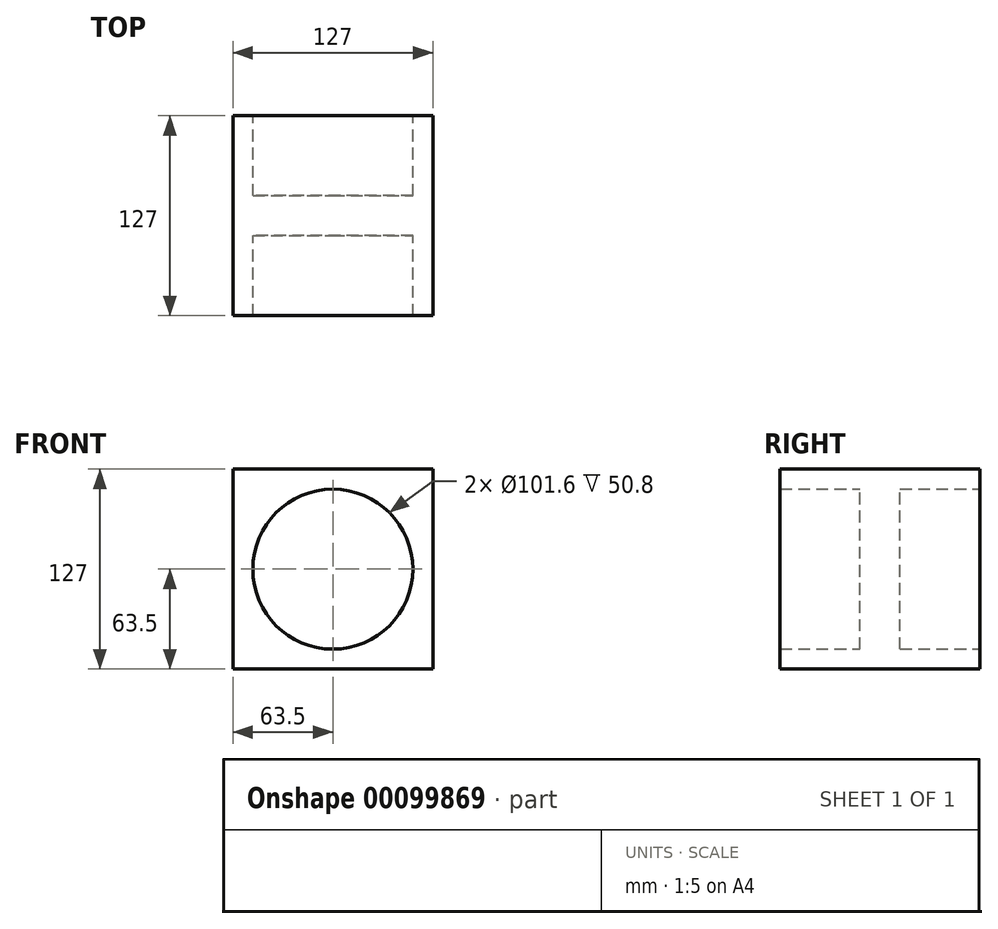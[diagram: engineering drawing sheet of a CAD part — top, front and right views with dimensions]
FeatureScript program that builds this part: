
annotation { "Feature Type Name" : "Feature", "Feature Type Description" : "" }
export const myFeature = defineFeature(function(context is Context, id is Id, definition is map)
    precondition{}
    {
        {
            var Q0;
            Q0=qCreatedBy(makeId("Front.planeOp"),FACE);
            var sketch = newSketch(context, id + "F0", { "sketchPlane" : qUnion([Q0])});
            skLineSegment(sketch, "E0.bottom", {"start": v(-63.5, 63.5) * mm, "end": v(63.5, 63.5) * mm});
            skLineSegment(sketch, "E0.top", {"start": v(-63.5, -63.5) * mm, "end": v(63.5, -63.5) * mm});
            skLineSegment(sketch, "E0.left", {"start": v(-63.5, 63.5) * mm, "end": v(-63.5, -63.5) * mm});
            skLineSegment(sketch, "E0.right", {"start": v(63.5, 63.5) * mm, "end": v(63.5, -63.5) * mm});
            skPoint(sketch, "E0.middle", {"position": v(0, 0) * mm});
            skCircle(sketch, "E1", {"center": v(0, 0) * mm, "radius": 50.8 * mm});
            skSolve(sketch);
        }
        {
            var Q0;
            Q0=makeQuery(id+"F0.imprint","IMPRINT",FACE,{"disambiguationData":[TD([[makeQuery(id+"F0.imprint","IMPRINT",EDGE,{"derivedFrom":sQuery(id+"F0.wireOp",EDGE,"E0.bottom")}),-1.0]])]});
            extrude(context, id + "F1", {"entities" : qUnion([Q0]), "endBound" : BoundingType.SYMMETRIC, "depth" : 127 * mm});
        }
        {
            var Q0;
            Q0=makeQuery(id+"F0.imprint","IMPRINT",FACE,{"disambiguationData":[TD([[makeQuery(id+"F0.imprint","IMPRINT",EDGE,{"derivedFrom":sQuery(id+"F0.wireOp",EDGE,"E1")}),1.0]])]});
            extrude(context, id + "F2", {"entities" : qUnion([Q0]), "operationType" : NewBodyOperationType.ADD, "endBound" : BoundingType.SYMMETRIC, "depth" : 25.4 * mm});
        }
    });
